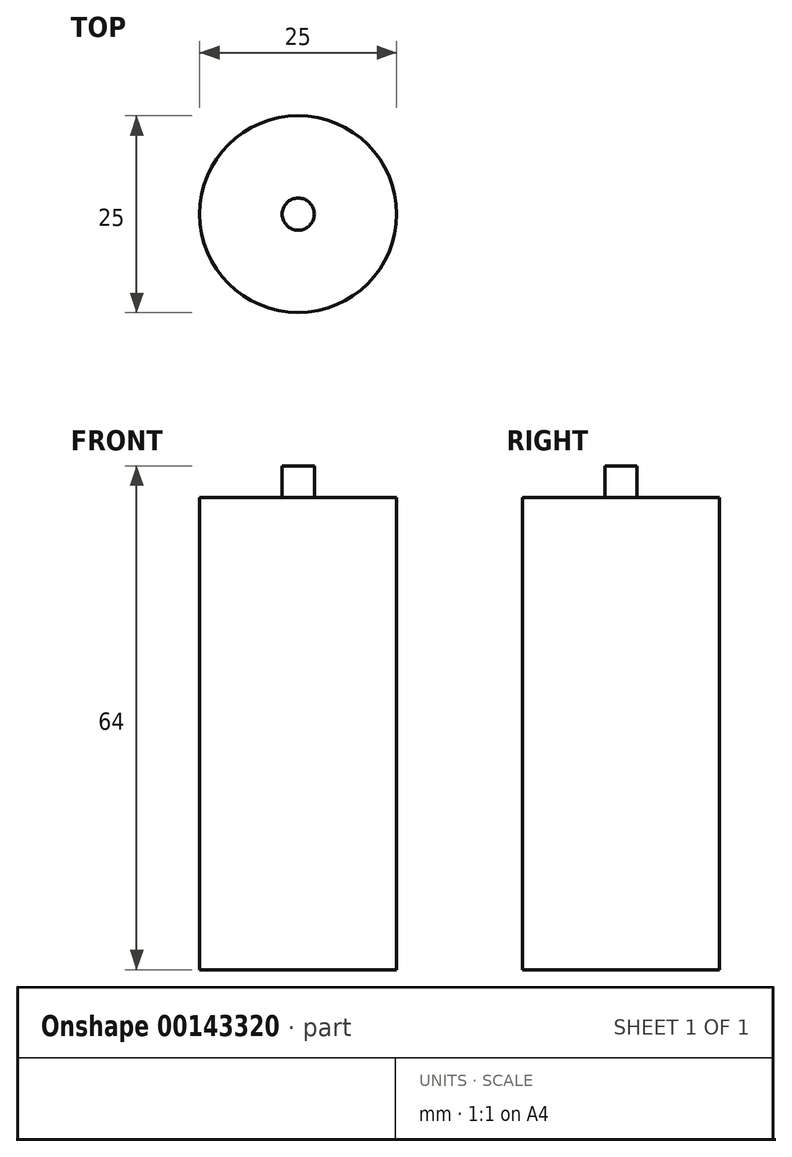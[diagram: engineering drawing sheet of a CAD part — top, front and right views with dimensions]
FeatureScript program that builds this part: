
annotation { "Feature Type Name" : "Feature", "Feature Type Description" : "" }
export const myFeature = defineFeature(function(context is Context, id is Id, definition is map)
    precondition{}
    {
        {
            var Q0;
            Q0=qCreatedBy(makeId("Top.planeOp"),FACE);
            var sketch = newSketch(context, id + "F0", { "sketchPlane" : qUnion([Q0])});
            skCircle(sketch, "E0", {"center": v(0, 0) * mm, "radius": 12.5 * mm});
            skCircle(sketch, "E1", {"center": v(0, 0) * mm, "radius": 2.04 * mm});
            skLineSegment(sketch, "E2.bottom", {"start": v(8.76, -8.92) * mm, "end": v(-8.76, -8.92) * mm});
            skLineSegment(sketch, "E2.top", {"start": v(8.76, 8.92) * mm, "end": v(-8.76, 8.92) * mm});
            skLineSegment(sketch, "E2.left", {"start": v(8.76, -8.92) * mm, "end": v(8.76, 8.92) * mm});
            skLineSegment(sketch, "E2.right", {"start": v(-8.76, -8.92) * mm, "end": v(-8.76, 8.92) * mm});
            skSolve(sketch);
        }
        {
            var Q0;
            Q0=makeQuery(id+"F0.imprint","IMPRINT",FACE,{"disambiguationData":[TD([[makeQuery(id+"F0.imprint","IMPRINT",EDGE,{"derivedFrom":sQuery(id+"F0.wireOp",EDGE,"E0")}),1.0]])]});
            var Q1;
            Q1=makeQuery(id+"F0.imprint","IMPRINT",FACE,{"disambiguationData":[TD([[makeQuery(id+"F0.imprint","IMPRINT",EDGE,{"derivedFrom":sQuery(id+"F0.wireOp",EDGE,"E1")}),-1.0]])]});
            extrude(context, id + "F1", {"entities" : qUnion([Q0, Q1]), "depth" : 60 * mm});
        }
        {
            var Q0;
            Q0=makeQuery(id+"F0.imprint","IMPRINT",FACE,{"disambiguationData":[TD([[makeQuery(id+"F0.imprint","IMPRINT",EDGE,{"derivedFrom":sQuery(id+"F0.wireOp",EDGE,"E1")}),1.0]])]});
            extrude(context, id + "F2", {"entities" : qUnion([Q0]), "operationType" : NewBodyOperationType.ADD, "depth" : 64 * mm});
        }
    });
